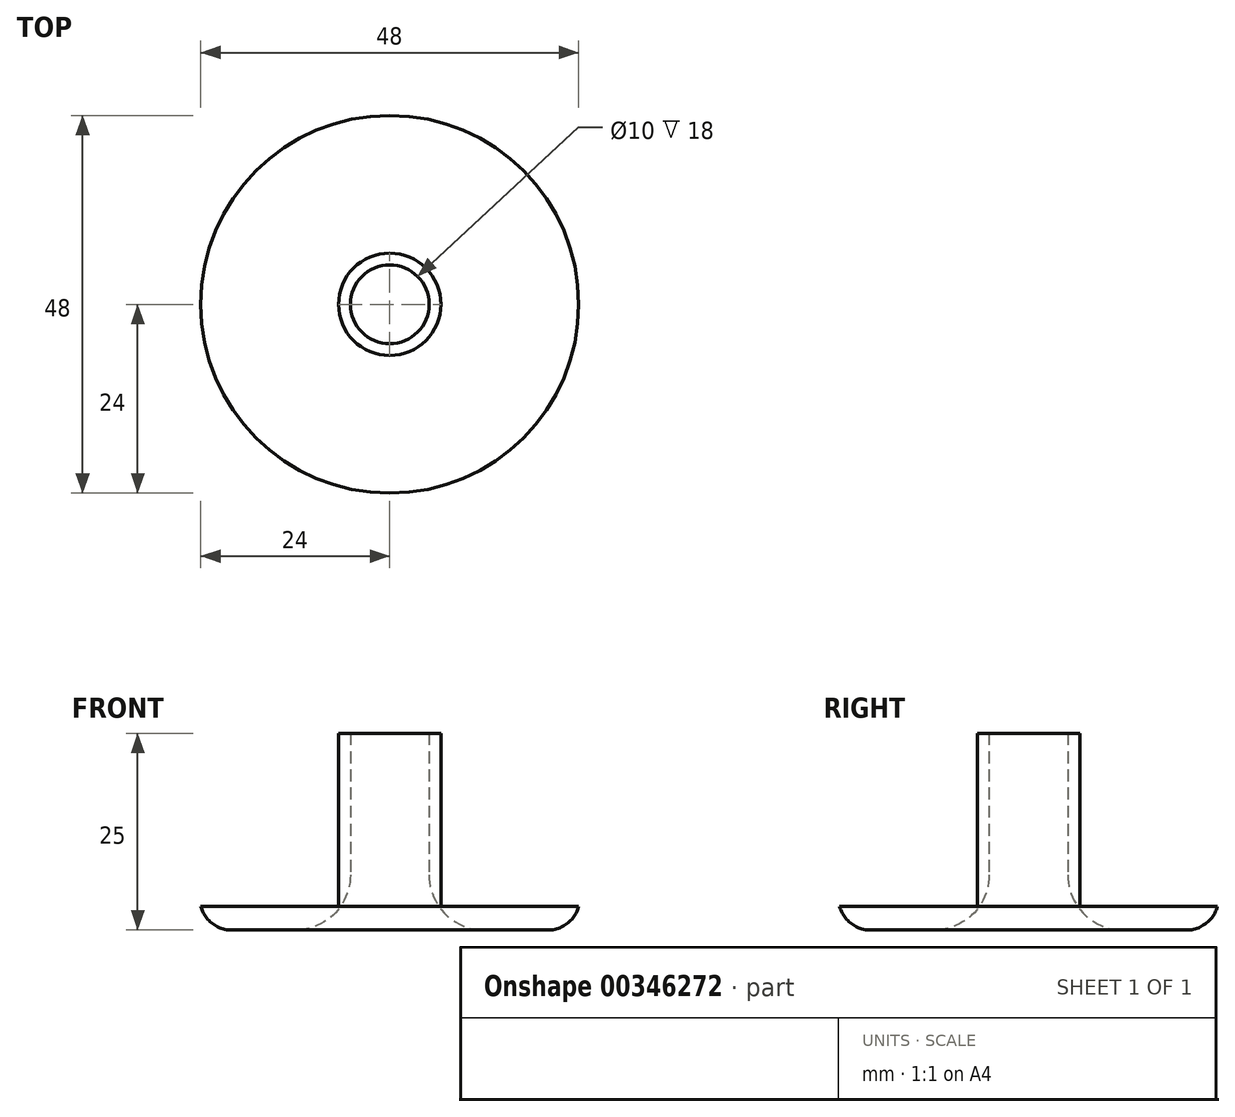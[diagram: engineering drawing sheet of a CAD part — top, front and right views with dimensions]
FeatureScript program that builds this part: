
annotation { "Feature Type Name" : "Feature", "Feature Type Description" : "" }
export const myFeature = defineFeature(function(context is Context, id is Id, definition is map)
    precondition{}
    {
        {
            var Q0;
            Q0=qCreatedBy(makeId("Top.planeOp"),FACE);
            var sketch = newSketch(context, id + "F0", { "sketchPlane" : qUnion([Q0])});
            skCircle(sketch, "E0", {"center": v(0, 0) * mm, "radius": 24 * mm});
            skCircle(sketch, "E1", {"center": v(0, 0) * mm, "radius": 5 * mm});
            skCircle(sketch, "E2", {"center": v(0, 0) * mm, "radius": 6.5 * mm});
            skSolve(sketch);
        }
        {
            var Q0;
            Q0 = qSketchRegion(id + "F0", true);
            extrude(context, id + "F1", {"entities" : qUnion([Q0]), "depth" : 3 * mm});
        }
        {
            var Q0;
            Q0=makeQuery(id+"F0.imprint","IMPRINT",FACE,{"disambiguationData":[TD([[makeQuery(id+"F0.imprint","IMPRINT",EDGE,{"derivedFrom":sQuery(id+"F0.wireOp",EDGE,"E1")}),-1.0]])]});
            extrude(context, id + "F2", {"entities" : qUnion([Q0]), "operationType" : NewBodyOperationType.ADD, "depth" : 25 * mm});
        }
        {
            var Q0;
            Q0=makeQuery(id+"F2.opExtrude","CAP_EDGE",EDGE,{"disambiguationData":[OSD([sQuery(id+"F0.wireOp",EDGE,"E1")])],"isStart":true});
            fillet(context, id + "F3", {"entities" : qUnion([Q0]), "radius" : 7 * mm, "tangentPropagation" : true, "allowEdgeOverflow" : false});
        }
        {
            var Q0;
            Q0=makeQuery(id+"F1.opExtrude","CAP_EDGE",EDGE,{"disambiguationData":[OSD([sQuery(id+"F0.wireOp",EDGE,"E0")])],"isStart":true});
            fillet(context, id + "F4", {"entities" : qUnion([Q0]), "radius" : 4.1 * mm, "tangentPropagation" : true, "allowEdgeOverflow" : false});
        }
    });
